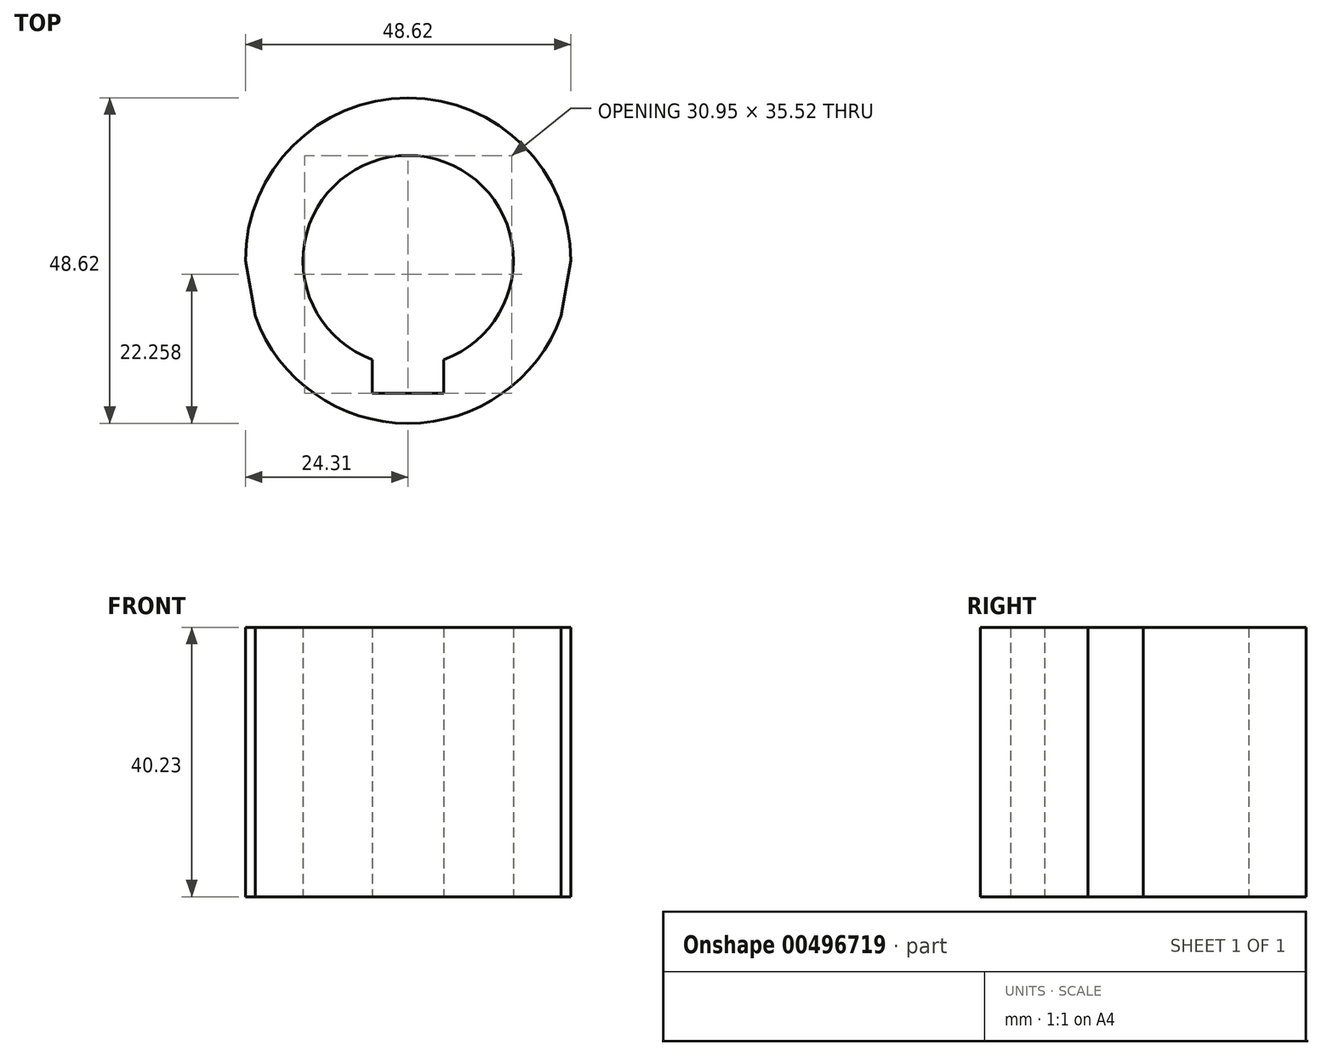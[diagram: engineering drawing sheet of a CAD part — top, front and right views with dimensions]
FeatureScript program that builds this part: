
annotation { "Feature Type Name" : "Feature", "Feature Type Description" : "" }
export const myFeature = defineFeature(function(context is Context, id is Id, definition is map)
    precondition{}
    {
        {
            var Q0;
            Q0=qCreatedBy(makeId("Top.planeOp"),FACE);
            var sketch = newSketch(context, id + "F0", { "sketchPlane" : qUnion([Q0])});
            skCircle(sketch, "E0", {"center": v(0, 0) * mm, "radius": 24.3 * mm});
            skCircle(sketch, "E1", {"center": v(0, 0) * mm, "radius": 15.7 * mm});
            skLineSegment(sketch, "E2.bottom", {"start": v(5.33, 19.81) * mm, "end": v(-5.33, 19.81) * mm});
            skLineSegment(sketch, "E2.top", {"start": v(5.33, -19.81) * mm, "end": v(-5.33, -19.81) * mm});
            skLineSegment(sketch, "E2.left", {"start": v(5.33, 19.81) * mm, "end": v(5.33, -19.81) * mm});
            skLineSegment(sketch, "E2.right", {"start": v(-5.33, 19.81) * mm, "end": v(-5.33, -19.81) * mm});
            skCircle(sketch, "E3", {"center": v(0, -63.28) * mm, "radius": 5.33 * mm});
            skCircle(sketch, "E4", {"center": v(0, -63.28) * mm, "radius": 13 * mm});
            skLineSegment(sketch, "E5", {"start": v(-24.3, 0) * mm, "end": v(-12.81, -65.52) * mm});
            skLineSegment(sketch, "E6.MirrorCS", {"start": v(24.3, 0) * mm, "end": v(12.81, -65.52) * mm});
            skSolve(sketch);
        }
        {
            var Q0;
            {var subQ6=sQuery(id+"F0.wireOp",EDGE,"E2.bottom");Q0=makeQuery(id+"F0.imprint","IMPRINT",FACE,{"disambiguationData":[TD([[makeQuery(id+"F0.imprint","IMPRINT",EDGE,{"derivedFrom":subQ6}),-1.0]])]});}
            var Q1;
            {var subQ5=sQuery(id+"F0.wireOp",EDGE,"E2.bottom");Q1=makeQuery(id+"F0.imprint","IMPRINT",FACE,{"disambiguationData":[TD([[makeQuery(id+"F0.imprint","IMPRINT",EDGE,{"derivedFrom":subQ5}),1.0]])]});}
            var Q2;
            {var subQ0=sQuery(id+"F0.wireOp",EDGE,"E6.MirrorCS");var subQ1=sQuery(id+"F0.wireOp",EDGE,"E0");var subQ2=makeQuery(id+"F0.imprint","INTERSECT",VERTEX,{"disambiguationData":[OD(0.0)],"derivedFrom":[subQ1,subQ0]});Q2=makeQuery(id+"F0.imprint","IMPRINT",FACE,{"disambiguationData":[TD([[makeQuery(id+"F0.imprint","IMPRINT",EDGE,{"disambiguationData":[TD([[subQ2,1.0]])],"derivedFrom":subQ1}),1.0]])]});}
            var Q3;
            {var subQ0=sQuery(id+"F0.wireOp",EDGE,"E5");var subQ1=sQuery(id+"F0.wireOp",EDGE,"E0");var subQ2=makeQuery(id+"F0.imprint","INTERSECT",VERTEX,{"disambiguationData":[OD(0.0)],"derivedFrom":[subQ1,subQ0]});Q3=makeQuery(id+"F0.imprint","IMPRINT",FACE,{"disambiguationData":[TD([[makeQuery(id+"F0.imprint","IMPRINT",EDGE,{"disambiguationData":[TD([[subQ2,-1.0]])],"derivedFrom":subQ1}),1.0]])]});}
            extrude(context, id + "F1", {"entities" : qUnion([Q0, Q1, Q2, Q3]), "depth" : 40.23 * mm});
        }
    });
